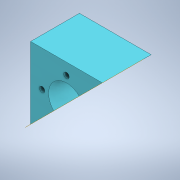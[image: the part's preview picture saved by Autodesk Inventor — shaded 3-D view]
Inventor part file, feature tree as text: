
AUTODESK INVENTOR PART (.ipt)
format: ipt  version: 2022.1 (Build 261234000, 234)  size: 957,952 bytes
history: native  units: mm
features: sketch x7, extrude x2, revolve x2, emboss x2, hole x1, plane x1, split x1
ambient origin geometry x8: Origin, YZ Plane, XZ Plane, XY Plane, X Axis, Y Axis, Z Axis, Center Point
bodies: Solid7 (feature_tree)
feature tree (16):
  extrude  "Extrusion20"  Depth=50.0mm
  revolve  "Revolution4"  [1 undecoded]
  extrude  "Extrusion21"  TaperAngle=90.0deg  [1 undecoded]
  revolve  "Revolution5"  [1 undecoded]
  hole  "Hole2"  [1 undecoded]
  plane  "Work Plane6"
  emboss  "Emboss3"
  emboss  "Emboss4"
  split  "Split1"
  sketch  "Sketch27"  dims[d124=50.0mm d125=50.0mm]
  sketch  "Sketch28"  dims[d126=29.0mm d127=0.0mm d128=3.0mm]
  sketch  "Sketch29"  dims[d129=12.5mm d130=90.0deg]
  sketch  "Sketch30"  dims[d131=5.0mm d132=0.0mm d133=2.5mm]
  sketch  "Sketch31"  dims[d134=90.0deg d135=34.0mm]
  sketch  "Sketch32"  dims[d136=34.0mm]
  sketch  "Sketch33"  dims[d137=3.797mm d138=6.0mm d139=11.43mm d140=15.24mm d141=14.3117mm d142=8.0mm d143=20.594885mm d144=1.0mm d145=0.0mm d146=1.0mm d147=0.0mm]
note: 4 required parameter values undecoded (feature->parameter linkage not recoverable at this tier; creation-order binding heuristic only, values carry confidence <= 0.55)